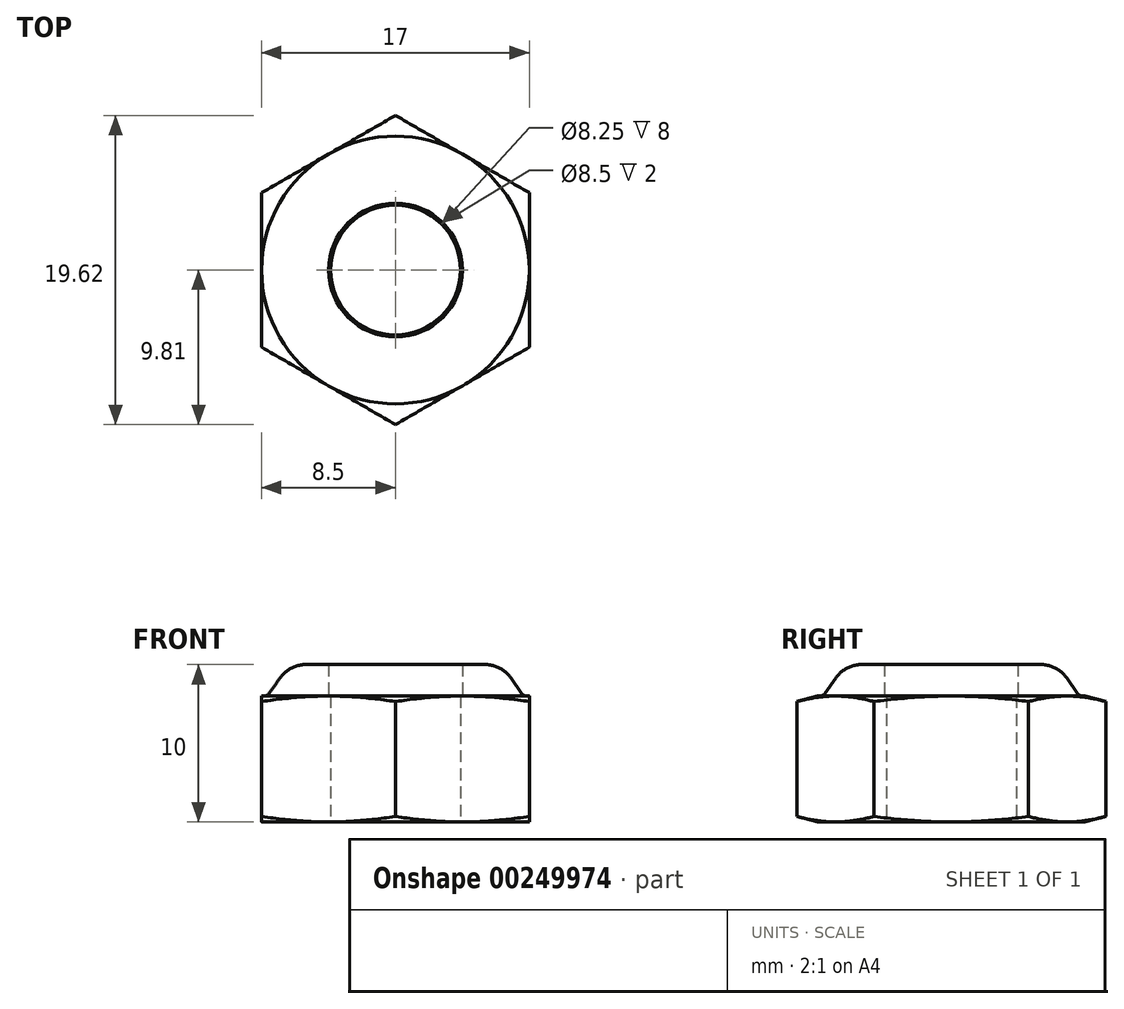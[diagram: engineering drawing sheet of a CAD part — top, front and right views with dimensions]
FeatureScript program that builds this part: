
annotation { "Feature Type Name" : "Feature", "Feature Type Description" : "" }
export const myFeature = defineFeature(function(context is Context, id is Id, definition is map)
    precondition{}
    {
        {
            var Q0;
            Q0=qCreatedBy(makeId("Top.planeOp"),FACE);
            var sketch = newSketch(context, id + "F0", { "sketchPlane" : qUnion([Q0])});
            skCircle(sketch, "E0.cCircle", {"center": v(0, 0) * mm, "radius": 8.5 * mm, "construction": true});
            skLineSegment(sketch, "E0.0", {"start": v(8.5, 4.9) * mm, "end": v(8.5, -4.9) * mm});
            skLineSegment(sketch, "E0.1", {"start": v(8.5, -4.9) * mm, "end": v(0, -9.81) * mm});
            skLineSegment(sketch, "E0.2", {"start": v(0, -9.81) * mm, "end": v(-8.5, -4.9) * mm});
            skLineSegment(sketch, "E0.3", {"start": v(-8.5, -4.9) * mm, "end": v(-8.5, 4.9) * mm});
            skLineSegment(sketch, "E0.4", {"start": v(-8.5, 4.9) * mm, "end": v(0, 9.81) * mm});
            skLineSegment(sketch, "E0.5", {"start": v(0, 9.81) * mm, "end": v(8.5, 4.9) * mm});
            skPoint(sketch, "E0.0.midPoint", {"position": v(8.5, 0) * mm});
            skCircle(sketch, "E1", {"center": v(0, 0) * mm, "radius": 4.12 * mm});
            skLineSegment(sketch, "E2", {"start": v(-12.53, -7.23) * mm, "end": v(14.01, 8.09) * mm, "construction": true});
            skPoint(sketch, "E3", {"position": v(-7.36, -4.25) * mm});
            skPoint(sketch, "E4", {"position": v(-8.5, -4.9) * mm});
            skSolve(sketch);
        }
        {
            var Q0;
            Q0=qSketchRegion(id+"F0",true);
            extrude(context, id + "F1", {"entities" : qUnion([Q0]), "depth" : 8 * mm});
        }
        {
            var Q0;
            Q0=makeQuery(id+"F1.opExtrude","SWEPT_EDGE",EDGE,{"disambiguationData":[OSD([sQuery(id+"F0.wireOp",EDGE,"E0.2"),sQuery(id+"F0.wireOp",EDGE,"E0.3")])]});
            cPoint(context, id + "F2", {"entities" : qUnion([Q0]), "parameter" : 0.5});
        }
        {
            var Q0;
            Q0=makeQuery(id+"F1.opExtrude","SWEPT_EDGE",EDGE,{"disambiguationData":[OSD([sQuery(id+"F0.wireOp",EDGE,"E0.0"),sQuery(id+"F0.wireOp",EDGE,"E0.5")])]});
            cPoint(context, id + "F3", {"entities" : qUnion([Q0]), "parameter" : 0.5});
        }
        {
            var Q0;
            Q0=qCreatedBy(id+"F2",VERTEX);
            var Q1;
            Q1=qCreatedBy(id+"F3",VERTEX);
            var Q2;
            Q2=makeQuery(id+"F1.opExtrude","CAP_VERTEX",VERTEX,{"disambiguationData":[OSD([sQuery(id+"F0.wireOp",EDGE,"E0.0"),sQuery(id+"F0.wireOp",EDGE,"E0.5")])],"isStart":true});
            cPlane(context, id + "F4", {"entities" : qUnion([Q0, Q1, Q2]), "cplaneType" : CPlaneType.THREE_POINT, "offset" : 25 * mm, "width" : 150 * mm, "height" : 150 * mm});
        }
        {
            var Q0;
            Q0=qCreatedBy(id+"F4.planeOp",FACE);
            var sketch = newSketch(context, id + "F5", { "sketchPlane" : qUnion([Q0])});
            skPoint(sketch, "E5.0", {"position": v(-8.5, 0) * mm});
            skLineSegment(sketch, "E6", {"start": v(-2.9, -1.5) * mm, "end": v(-15.32, 1.83) * mm});
            skPoint(sketch, "E7", {"position": v(-9.81, 8) * mm});
            skPoint(sketch, "E8", {"position": v(-9.81, 4) * mm});
            skLineSegment(sketch, "E9", {"start": v(-13.9, 4) * mm, "end": v(7.47, 4) * mm, "construction": true});
            skLineSegment(sketch, "E10", {"start": v(-15.32, -1.5) * mm, "end": v(-2.9, -1.5) * mm});
            skLineSegment(sketch, "E11", {"start": v(0, -0.96) * mm, "end": v(0, 9.49) * mm, "construction": true});
            skPoint(sketch, "E12.trimOffspring.end.orphan", {"position": v(-9.81, 0) * mm});
            skLineSegment(sketch, "E13", {"start": v(-15.32, 1.83) * mm, "end": v(-15.32, -1.5) * mm});
            skPoint(sketch, "E14.end.orphan", {"position": v(-10.64, -1.5) * mm});
            skPoint(sketch, "E14.start.orphan", {"position": v(-10.64, 0.57) * mm});
            skPoint(sketch, "E15.MirrorCS.start.orphan", {"position": v(-10.64, 7.43) * mm});
            skLineSegment(sketch, "E16.MirrorCS", {"start": v(-15.32, 6.17) * mm, "end": v(-15.32, 9.5) * mm});
            skLineSegment(sketch, "E17.MirrorCS", {"start": v(-2.9, 9.5) * mm, "end": v(-15.32, 6.17) * mm});
            skLineSegment(sketch, "E18.MirrorCS", {"start": v(-15.32, 9.5) * mm, "end": v(-2.9, 9.5) * mm});
            skPoint(sketch, "E19.MirrorP", {"position": v(-8.5, 8) * mm});
            skSolve(sketch);
        }
        {
            var Q0;
            Q0=makeQuery(id+"F5.imprint","IMPRINT",FACE,{"disambiguationData":[TD([[makeQuery(id+"F5.imprint","IMPRINT",EDGE,{"derivedFrom":sQuery(id+"F5.wireOp",EDGE,"E16.MirrorCS")}),-1.0]])]});
            var Q1;
            Q1=makeQuery(id+"F5.imprint","IMPRINT",FACE,{"disambiguationData":[TD([[makeQuery(id+"F5.imprint","IMPRINT",EDGE,{"derivedFrom":sQuery(id+"F5.wireOp",EDGE,"E6")}),1.0]])]});
            var Q2;
            Q2=sQuery(id+"F5.wireOp",EDGE,"E11");
            revolve(context, id + "F6", {"operationType" : NewBodyOperationType.REMOVE, "entities" : qUnion([Q0, Q1]), "axis" : qUnion([Q2]), "revolveType" : RevolveType.FULL, "oppositeDirection" : true});
        }
        {
            var Q0;
            Q0=qCreatedBy(makeId("Front.planeOp"),FACE);
            var sketch = newSketch(context, id + "F7", { "sketchPlane" : qUnion([Q0])});
            skLineSegment(sketch, "E20", {"start": v(-4.25, 8) * mm, "end": v(-4.25, 10) * mm});
            skLineSegment(sketch, "E21", {"start": v(-4.25, 8) * mm, "end": v(-8.34, 8) * mm});
            skLineSegment(sketch, "E22.0", {"start": v(-8.5, 8) * mm, "end": v(-8.34, 8) * mm});
            skLineSegment(sketch, "E23", {"start": v(-7.33, 9.15) * mm, "end": v(-8.01, 8.17) * mm});
            skArc(sketch, "E24.filletArc", {"start": v(-8.34, 8) * mm, "mid": v(-8.16, 8.05) * mm, "end": v(-8.01, 8.17) * mm});
            skLineSegment(sketch, "E25", {"start": v(-4.25, 10) * mm, "end": v(-5.7, 10) * mm});
            skArc(sketch, "E26.filletArc", {"start": v(-5.7, 10) * mm, "mid": v(-6.62, 9.77) * mm, "end": v(-7.33, 9.15) * mm});
            skSolve(sketch);
        }
        {
            var Q0;
            Q0 = qSketchRegion(id + "F7", true);
            var Q1;
            Q1=sQuery(id+"F5.wireOp",EDGE,"E11");
            revolve(context, id + "F8", {"operationType" : NewBodyOperationType.ADD, "entities" : qUnion([Q0]), "axis" : qUnion([Q1]), "revolveType" : RevolveType.FULL});
        }
    });
